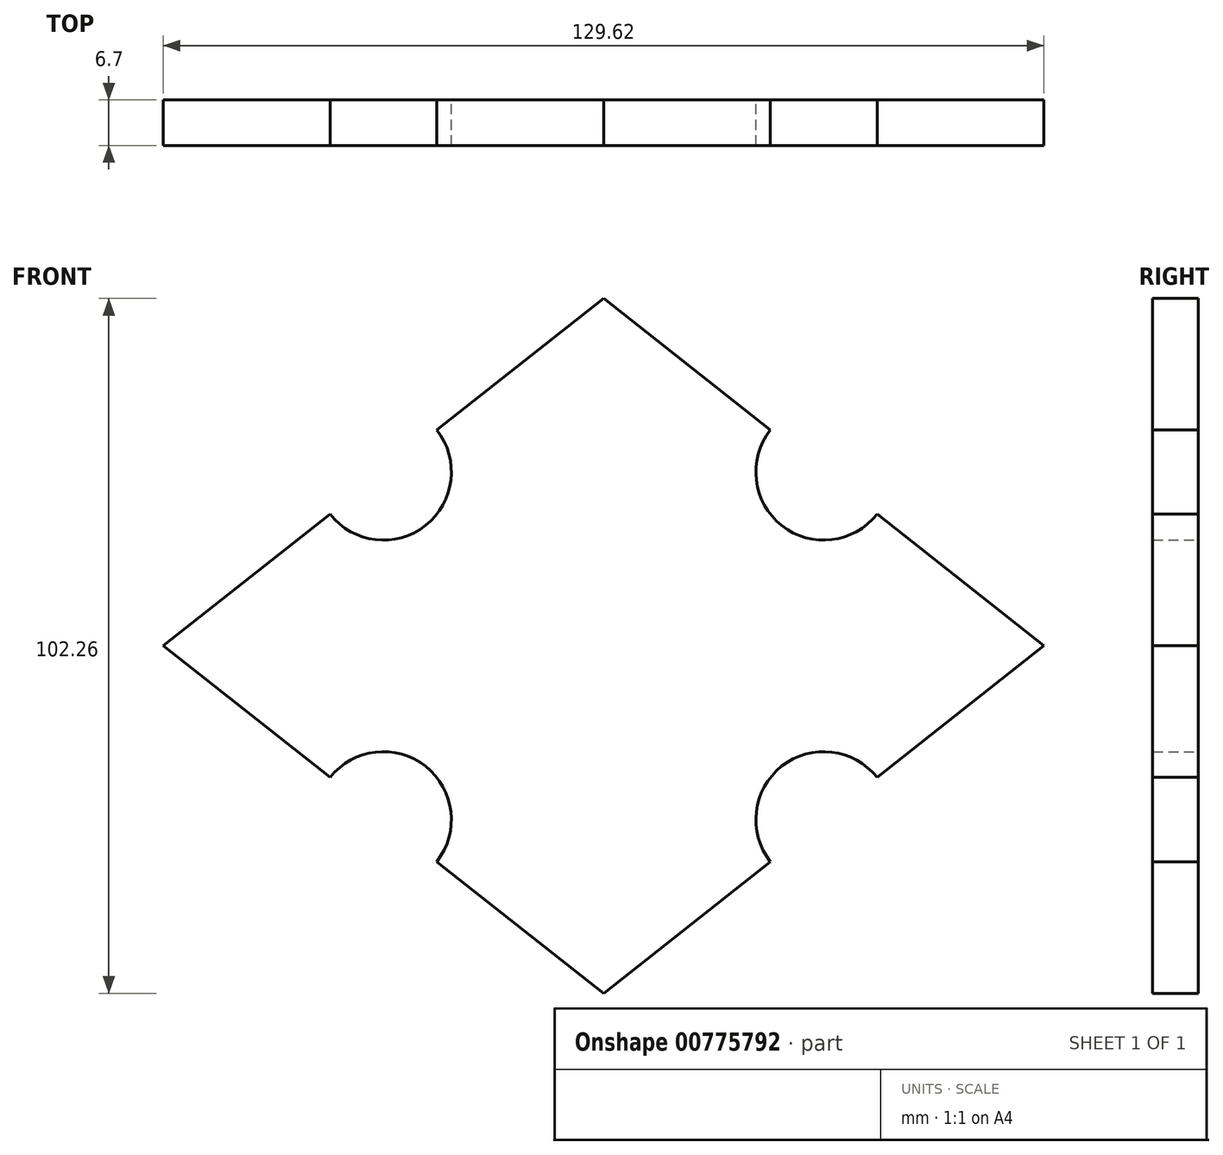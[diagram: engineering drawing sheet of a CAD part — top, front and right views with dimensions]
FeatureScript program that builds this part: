
annotation { "Feature Type Name" : "Feature", "Feature Type Description" : "" }
export const myFeature = defineFeature(function(context is Context, id is Id, definition is map)
    precondition{}
    {
        {
            var Q0;
            Q0=qCreatedBy(makeId("Front.planeOp"),FACE);
            var sketch = newSketch(context, id + "F0", { "sketchPlane" : qUnion([Q0])});
            skLineSegment(sketch, "E0.bottom", {"start": v(-64.8, 51.13) * mm, "end": v(64.8, 51.13) * mm});
            skLineSegment(sketch, "E0.top", {"start": v(-64.8, -51.13) * mm, "end": v(64.8, -51.13) * mm});
            skLineSegment(sketch, "E0.left", {"start": v(-64.8, 51.13) * mm, "end": v(-64.8, -51.13) * mm});
            skLineSegment(sketch, "E0.right", {"start": v(64.8, 51.13) * mm, "end": v(64.8, -51.13) * mm});
            skPoint(sketch, "E0.middle", {"position": v(0, 0) * mm});
            skLineSegment(sketch, "E1", {"start": v(0, 51.13) * mm, "end": v(24.55, 31.76) * mm});
            skLineSegment(sketch, "E2", {"start": v(64.8, 0) * mm, "end": v(40.25, -19.37) * mm});
            skLineSegment(sketch, "E3", {"start": v(0, -51.13) * mm, "end": v(-24.55, -31.76) * mm});
            skLineSegment(sketch, "E4", {"start": v(-64.8, 0) * mm, "end": v(-40.25, 19.37) * mm});
            skLineSegment(sketch, "E5", {"start": v(0, 51.13) * mm, "end": v(-24.55, 31.76) * mm, "construction": true});
            skLineSegment(sketch, "E6", {"start": v(64.8, 0) * mm, "end": v(40.25, -19.37) * mm, "construction": true});
            skLineSegment(sketch, "E7", {"start": v(0, 51.13) * mm, "end": v(24.55, 31.76) * mm, "construction": true});
            skArc(sketch, "E8", {"start": v(-40.25, 19.37) * mm, "mid": v(-26.2, 17.71) * mm, "end": v(-24.55, 31.76) * mm});
            skArc(sketch, "E9", {"start": v(24.55, 31.76) * mm, "mid": v(26.2, 17.71) * mm, "end": v(40.25, 19.37) * mm});
            skArc(sketch, "E10", {"start": v(40.25, -19.37) * mm, "mid": v(26.2, -17.71) * mm, "end": v(24.55, -31.76) * mm});
            skArc(sketch, "E11", {"start": v(-24.55, -31.76) * mm, "mid": v(-26.2, -17.71) * mm, "end": v(-40.25, -19.37) * mm});
            skLineSegment(sketch, "E12.trimOffspring", {"start": v(-24.55, 31.76) * mm, "end": v(0, 51.13) * mm});
            skLineSegment(sketch, "E13.trimOffspring", {"start": v(40.25, 19.37) * mm, "end": v(64.8, 0) * mm});
            skLineSegment(sketch, "E14.trimOffspring", {"start": v(24.55, -31.76) * mm, "end": v(0, -51.13) * mm});
            skLineSegment(sketch, "E15.trimOffspring", {"start": v(-40.25, -19.37) * mm, "end": v(-64.8, 0) * mm});
            skSolve(sketch);
        }
        {
            var Q0;
            Q0=makeQuery(id+"F0.imprint","IMPRINT",FACE,{"disambiguationData":[TD([[makeQuery(id+"F0.imprint","IMPRINT",EDGE,{"derivedFrom":sQuery(id+"F0.wireOp",EDGE,"E1")}),-1.0]])]});
            extrude(context, id + "F1", {"entities" : qUnion([Q0]), "depth" : 6.7 * mm, "offsetDistance" : 25 * mm});
        }
    });
